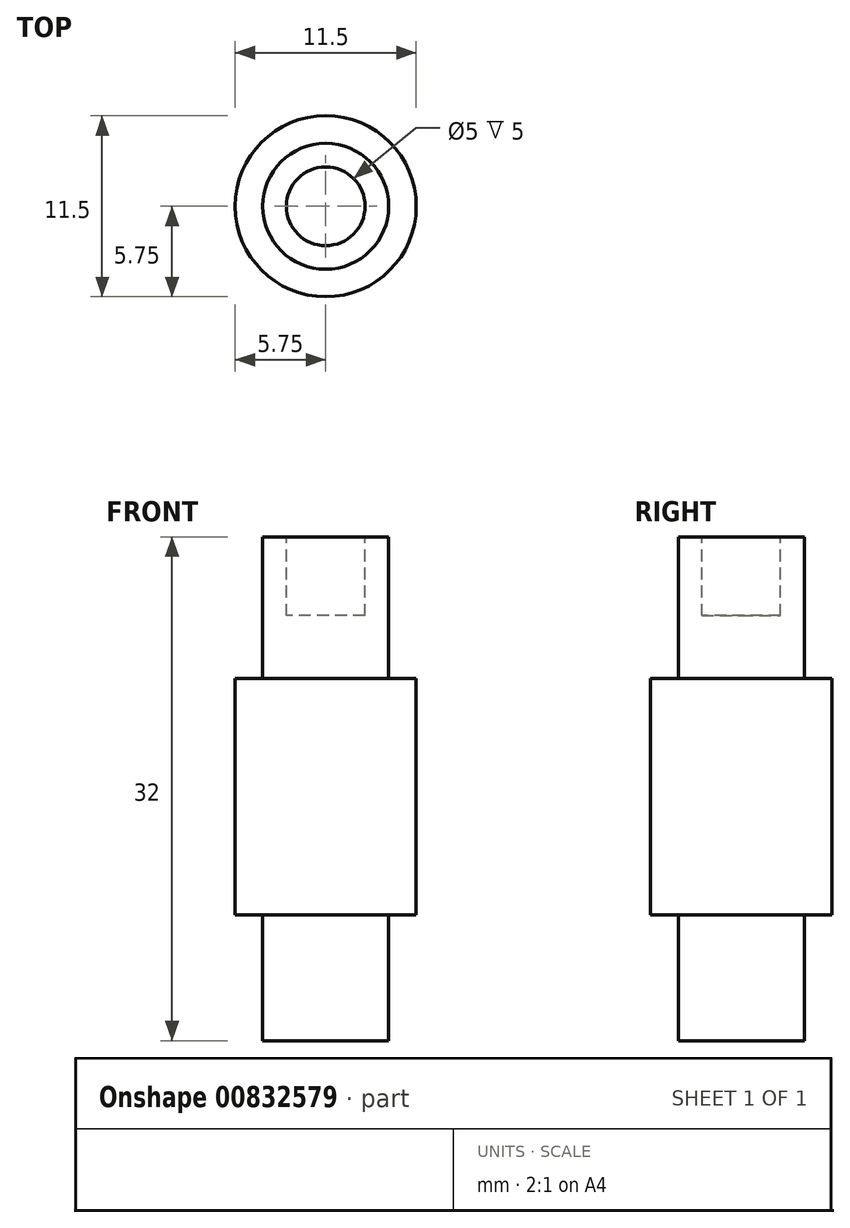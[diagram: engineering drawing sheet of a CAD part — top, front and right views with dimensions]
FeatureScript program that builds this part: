
annotation { "Feature Type Name" : "Feature", "Feature Type Description" : "" }
export const myFeature = defineFeature(function(context is Context, id is Id, definition is map)
    precondition{}
    {
        {
            var Q0;
            Q0=qCreatedBy(makeId("Top.planeOp"),FACE);
            var sketch = newSketch(context, id + "F0", { "sketchPlane" : qUnion([Q0])});
            skCircle(sketch, "E0", {"center": v(0, 0) * mm, "radius": 4 * mm});
            skSolve(sketch);
        }
        {
            var Q0;
            Q0=makeQuery(id+"F0.imprint","IMPRINT",FACE,{"disambiguationData":[TD([[makeQuery(id+"F0.imprint","IMPRINT",EDGE,{"derivedFrom":sQuery(id+"F0.wireOp",EDGE,"E0")}),1.0]])]});
            extrude(context, id + "F1", {"entities" : qUnion([Q0]), "depth" : 8 * mm, "offsetDistance" : 25 * mm});
        }
        {
            var Q0;
            Q0=makeQuery(id+"F1.opExtrude","CAP_FACE",FACE,{"disambiguationData":[OSD([sQuery(id+"F0.wireOp",EDGE,"E0")])],"isStart":false});
            var sketch = newSketch(context, id + "F2", { "sketchPlane" : qUnion([Q0])});
            skCircle(sketch, "E1", {"center": v(0, 0) * mm, "radius": 5.75 * mm});
            skSolve(sketch);
        }
        {
            var Q0;
            Q0=makeQuery(id+"F2.imprint","IMPRINT",FACE,{"disambiguationData":[TD([[makeQuery(id+"F2.imprint","IMPRINT",EDGE,{"derivedFrom":sQuery(id+"F2.wireOp",EDGE,"E1")}),1.0]])]});
            var Q1;
            Q1=makeQuery(id+"F2.imprint","IMPRINT",FACE,{"disambiguationData":[TD([[makeQuery(id+"F2.imprint","IMPRINT",EDGE,{"derivedFrom":makeQuery(id+"F1.opExtrude","CAP_EDGE",EDGE,{"disambiguationData":[OSD([sQuery(id+"F0.wireOp",EDGE,"E0")])],"isStart":false})}),1.0]])]});
            extrude(context, id + "F3", {"entities" : qUnion([Q0, Q1]), "operationType" : NewBodyOperationType.ADD, "depth" : 15 * mm, "offsetDistance" : 25 * mm});
        }
        {
            var Q0;
            Q0=makeQuery(id+"F3.opExtrude","CAP_FACE",FACE,{"disambiguationData":[OSD([sQuery(id+"F2.wireOp",EDGE,"E1")])],"isStart":false});
            var sketch = newSketch(context, id + "F4", { "sketchPlane" : qUnion([Q0])});
            skCircle(sketch, "E2", {"center": v(0, 0) * mm, "radius": 4 * mm});
            skSolve(sketch);
        }
        {
            var Q0;
            Q0=makeQuery(id+"F4.imprint","IMPRINT",FACE,{"disambiguationData":[TD([[makeQuery(id+"F4.imprint","IMPRINT",EDGE,{"derivedFrom":sQuery(id+"F4.wireOp",EDGE,"E2")}),1.0]])]});
            extrude(context, id + "F5", {"entities" : qUnion([Q0]), "operationType" : NewBodyOperationType.ADD, "depth" : 9 * mm, "offsetDistance" : 25 * mm});
        }
        {
            var Q0;
            Q0=makeQuery(id+"F5.opExtrude","CAP_FACE",FACE,{"disambiguationData":[OSD([sQuery(id+"F4.wireOp",EDGE,"E2")])],"isStart":false});
            var sketch = newSketch(context, id + "F6", { "sketchPlane" : qUnion([Q0])});
            skCircle(sketch, "E3", {"center": v(0, 0) * mm, "radius": 2.5 * mm});
            skSolve(sketch);
        }
        {
            var Q0;
            Q0=makeQuery(id+"F6.imprint","IMPRINT",FACE,{"disambiguationData":[TD([[makeQuery(id+"F6.imprint","IMPRINT",EDGE,{"derivedFrom":sQuery(id+"F6.wireOp",EDGE,"E3")}),1.0]])]});
            extrude(context, id + "F7", {"entities" : qUnion([Q0]), "operationType" : NewBodyOperationType.REMOVE, "oppositeDirection" : true, "depth" : 5 * mm, "offsetDistance" : 25 * mm});
        }
    });
